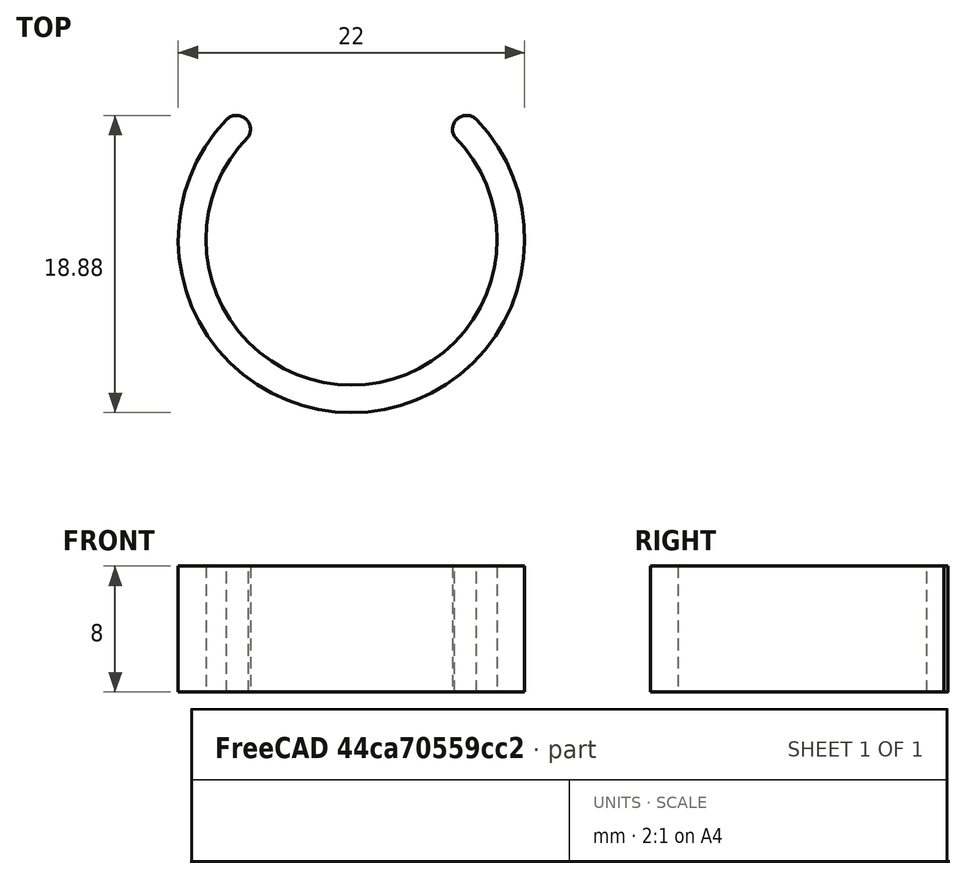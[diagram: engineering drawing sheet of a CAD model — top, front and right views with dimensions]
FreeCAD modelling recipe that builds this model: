
FCSTD DOCUMENT  (FreeCAD 0.21R33771 (Git))
Label: net_clip
License: All rights reserved
LicenseURL: http://en.wikipedia.org/wiki/All_rights_reserved
objects: Sketcher::SketchObject×1, PartDesign::Pad×1, PartDesign::Body×1
note: 4 computed .brp shape members not serialized (recipe doc carries the construction recipe); baked Part::Feature solids carry a one-line shape summary decoded from their .brp

FEATURE [Sketcher::SketchObject] Sketch
  FullyConstrained = false
  MapMode = 5
  Support = -> [XY_Plane]
  sketch-geometry (6):
    g0: ArcOfCircle CenterX=0 CenterY=0 CenterZ=0 NormalX=0 NormalY=0 NormalZ=1 AngleXU=0 Radius=9.25 StartAngle=2.35619 EndAngle=7.06858
    g1: ArcOfCircle CenterX=0 CenterY=0 CenterZ=0 NormalX=0 NormalY=0 NormalZ=1 AngleXU=0 Radius=11 StartAngle=2.37647 EndAngle=7.04831
    g2: LineSegment StartX=0 StartY=0 StartZ=0 EndX=-6.54074 EndY=6.54074 EndZ=0
    g3: LineSegment StartX=0 StartY=0 StartZ=0 EndX=6.54074 EndY=6.54074 EndZ=0
    g4: ArcOfCircle CenterX=-7.30493 CenterY=6.99266 CenterZ=0 NormalX=0 NormalY=0 NormalZ=1 AngleXU=0 Radius=0.88782 StartAngle=5.74914 EndAngle=8.6418
    g5: ArcOfCircle CenterX=7.30493 CenterY=6.99266 CenterZ=0 NormalX=0 NormalY=0 NormalZ=1 AngleXU=0 Radius=0.88782 StartAngle=0.782979 EndAngle=3.67564
  constraints (15):
    c: Coincident(g0,g-1)
    c: Coincident(g1,g0)
    c: Radius(g0) = 9.25
    c: Coincident(g2,g0)
    c: Coincident(g2,g0)
    c: Coincident(g3,g0)
    c: Coincident(g3,g0)
    c: Angle(g2) = 2.35619
    c: Angle(g3) = 0.785398
    c: Radius(g1) = 11
    c: Coincident(g4,g1)
    c: Coincident(g4,g0)
    c: Coincident(g5,g0)
    c: Coincident(g5,g1)
    c: Symmetric(g5,g4,g-2)
FEATURE [PartDesign::Pad] Pad
  Direction = (0,0,1)
  Length = 8
  Length2 = 10
  Profile = -> Sketch
  ReferenceAxis = -> Sketch [N_Axis]
  Type = 0
FEATURE [PartDesign::Body] Body
  Group = -> [Sketch,Pad]
  Origin = -> Origin
  Tip = -> Pad
